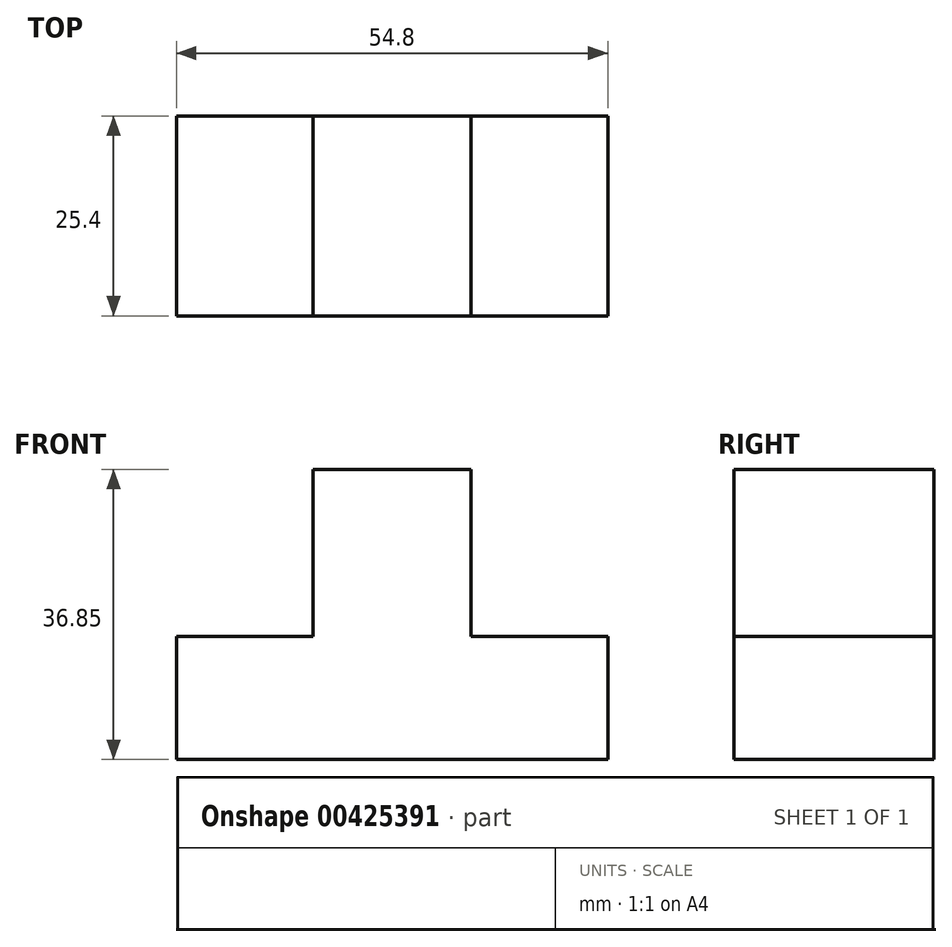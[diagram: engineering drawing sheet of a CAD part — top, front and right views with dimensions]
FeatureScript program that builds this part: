
annotation { "Feature Type Name" : "Feature", "Feature Type Description" : "" }
export const myFeature = defineFeature(function(context is Context, id is Id, definition is map)
    precondition{}
    {
        {
            var Q0;
            Q0=qCreatedBy(makeId("Front.planeOp"),FACE);
            var sketch = newSketch(context, id + "F0", { "sketchPlane" : qUnion([Q0])});
            skLineSegment(sketch, "E0", {"start": v(0, 15.66) * mm, "end": v(-17.38, 15.66) * mm});
            skLineSegment(sketch, "E1", {"start": v(-17.38, 15.66) * mm, "end": v(-17.38, 36.85) * mm});
            skLineSegment(sketch, "E2", {"start": v(-17.38, 36.85) * mm, "end": v(-37.43, 36.85) * mm});
            skLineSegment(sketch, "E3", {"start": v(-37.43, 36.85) * mm, "end": v(-37.43, 15.66) * mm});
            skLineSegment(sketch, "E4", {"start": v(-37.43, 15.66) * mm, "end": v(-54.8, 15.66) * mm});
            skLineSegment(sketch, "E5", {"start": v(-54.8, 15.66) * mm, "end": v(-54.8, 0) * mm});
            skLineSegment(sketch, "E6", {"start": v(-54.8, 0) * mm, "end": v(0, 0) * mm});
            skLineSegment(sketch, "E7", {"start": v(0, 0) * mm, "end": v(0, 15.66) * mm});
            skSolve(sketch);
        }
        {
            var Q0;
            Q0=makeQuery(id+"F0.imprint","IMPRINT",FACE,{"disambiguationData":[TD([[makeQuery(id+"F0.imprint","IMPRINT",EDGE,{"derivedFrom":sQuery(id+"F0.wireOp",EDGE,"E0")}),1.0]])]});
            extrude(context, id + "F1", {"entities" : qUnion([Q0]), "depth" : 25.4 * mm});
        }
    });
